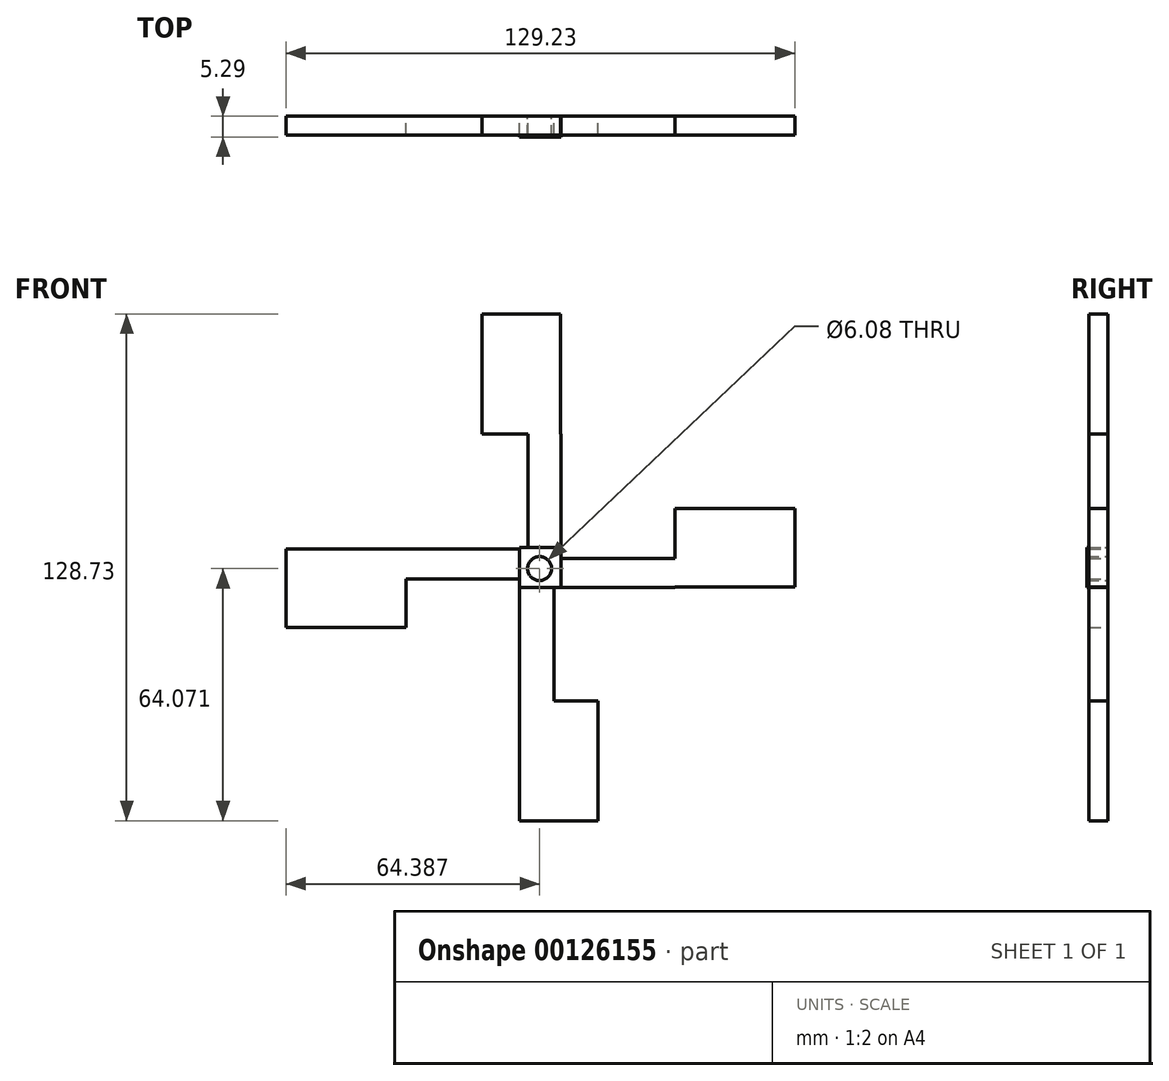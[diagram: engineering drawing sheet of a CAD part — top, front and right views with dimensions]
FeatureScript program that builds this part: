
annotation { "Feature Type Name" : "Feature", "Feature Type Description" : "" }
export const myFeature = defineFeature(function(context is Context, id is Id, definition is map)
    precondition{}
    {
        {
            var Q0;
            Q0=qCreatedBy(makeId("Front.planeOp"),FACE);
            var sketch = newSketch(context, id + "F0", { "sketchPlane" : qUnion([Q0])});
            skLineSegment(sketch, "E0.bottom", {"start": v(0, 0) * mm, "end": v(10.54, 0) * mm});
            skLineSegment(sketch, "E0.top", {"start": v(0, 10.1) * mm, "end": v(10.54, 10.1) * mm});
            skLineSegment(sketch, "E0.left", {"start": v(0, 0) * mm, "end": v(0, 10.1) * mm});
            skLineSegment(sketch, "E0.right", {"start": v(10.54, 0) * mm, "end": v(10.54, 10.1) * mm});
            skCircle(sketch, "E1", {"center": v(5.06, 4.74) * mm, "radius": 3.04 * mm});
            skSolve(sketch);
        }
        {
            var Q0;
            Q0=qCreatedBy(makeId("Front.planeOp"),FACE);
            var sketch = newSketch(context, id + "F1", { "sketchPlane" : qUnion([Q0])});
            skLineSegment(sketch, "E2.bottom", {"start": v(0, -28.85) * mm, "end": v(19.94, -28.85) * mm});
            skLineSegment(sketch, "E2.top", {"start": v(0, -59.33) * mm, "end": v(19.94, -59.33) * mm});
            skLineSegment(sketch, "E2.left", {"start": v(0, -28.85) * mm, "end": v(0, -59.33) * mm});
            skLineSegment(sketch, "E2.right", {"start": v(19.94, -28.85) * mm, "end": v(19.94, -59.33) * mm});
            skLineSegment(sketch, "E3.bottom", {"start": v(39.42, 20.01) * mm, "end": v(69.9, 20.01) * mm});
            skLineSegment(sketch, "E3.top", {"start": v(39.42, 0.08) * mm, "end": v(69.9, 0.08) * mm});
            skLineSegment(sketch, "E3.left", {"start": v(39.42, 20.01) * mm, "end": v(39.42, 0.08) * mm});
            skLineSegment(sketch, "E3.right", {"start": v(69.9, 20.01) * mm, "end": v(69.9, 0.08) * mm});
            skLineSegment(sketch, "E4.bottom", {"start": v(10.56, 0) * mm, "end": v(39.42, 0) * mm});
            skLineSegment(sketch, "E4.top", {"start": v(10.56, 7.32) * mm, "end": v(39.42, 7.32) * mm});
            skLineSegment(sketch, "E4.left", {"start": v(10.56, 0) * mm, "end": v(10.56, 7.32) * mm});
            skLineSegment(sketch, "E4.right", {"start": v(39.42, 0) * mm, "end": v(39.42, 7.32) * mm});
            skLineSegment(sketch, "E5.bottom", {"start": v(-28.85, 2.16) * mm, "end": v(0, 2.16) * mm});
            skLineSegment(sketch, "E5.top", {"start": v(-28.85, 9.68) * mm, "end": v(0, 9.68) * mm});
            skLineSegment(sketch, "E5.right", {"start": v(0, 2.16) * mm, "end": v(0, 9.68) * mm});
            skPoint(sketch, "E6.oppositeSnap0", {"position": v(9.97, -28.85) * mm});
            skLineSegment(sketch, "E6.bottom", {"start": v(0, -28.85) * mm, "end": v(9.97, -28.85) * mm});
            skLineSegment(sketch, "E6.top", {"start": v(0, 0) * mm, "end": v(9.97, 0) * mm});
            skLineSegment(sketch, "E6.left", {"start": v(0, -28.85) * mm, "end": v(0, 0) * mm});
            skLineSegment(sketch, "E7.bottom", {"start": v(-28.85, 9.68) * mm, "end": v(-59.33, 9.68) * mm});
            skLineSegment(sketch, "E7.top", {"start": v(-28.85, -10.26) * mm, "end": v(-59.33, -10.26) * mm});
            skLineSegment(sketch, "E7.left", {"start": v(-28.85, 9.68) * mm, "end": v(-28.85, -10.26) * mm});
            skLineSegment(sketch, "E7.right", {"start": v(-59.33, 9.68) * mm, "end": v(-59.33, -10.26) * mm});
            skLineSegment(sketch, "E8", {"start": v(10.54, 10.08) * mm, "end": v(10.54, 38.94) * mm});
            skLineSegment(sketch, "E9", {"start": v(2.1, 10.08) * mm, "end": v(2.1, 31.52) * mm});
            skLineSegment(sketch, "E10.bottom", {"start": v(-9.6, 38.92) * mm, "end": v(10.34, 38.92) * mm});
            skLineSegment(sketch, "E10.top", {"start": v(-9.6, 69.4) * mm, "end": v(10.34, 69.4) * mm});
            skLineSegment(sketch, "E10.left", {"start": v(-9.6, 38.92) * mm, "end": v(-9.6, 69.4) * mm});
            skLineSegment(sketch, "E10.right", {"start": v(10.34, 38.92) * mm, "end": v(10.34, 69.4) * mm});
            skLineSegment(sketch, "E11.bottom", {"start": v(2.1, 10.08) * mm, "end": v(10.54, 10.08) * mm});
            skLineSegment(sketch, "E11.top", {"start": v(2.1, 38.94) * mm, "end": v(10.54, 38.94) * mm});
            skLineSegment(sketch, "E11.left", {"start": v(2.1, 10.08) * mm, "end": v(2.1, 38.94) * mm});
            skLineSegment(sketch, "E12", {"start": v(8.72, 0) * mm, "end": v(8.72, -28.85) * mm});
            skSolve(sketch);
        }
        {
            var Q0;
            Q0 = qSketchRegion(id + "F0", true);
            extrude(context, id + "F2", {"entities" : qUnion([Q0]), "depth" : 5.3 * mm});
        }
        {
            var Q0;
            Q0 = qSketchRegion(id + "F1", true);
            extrude(context, id + "F3", {"entities" : qUnion([Q0]), "operationType" : NewBodyOperationType.ADD, "depth" : 4.76 * mm});
        }
    });
